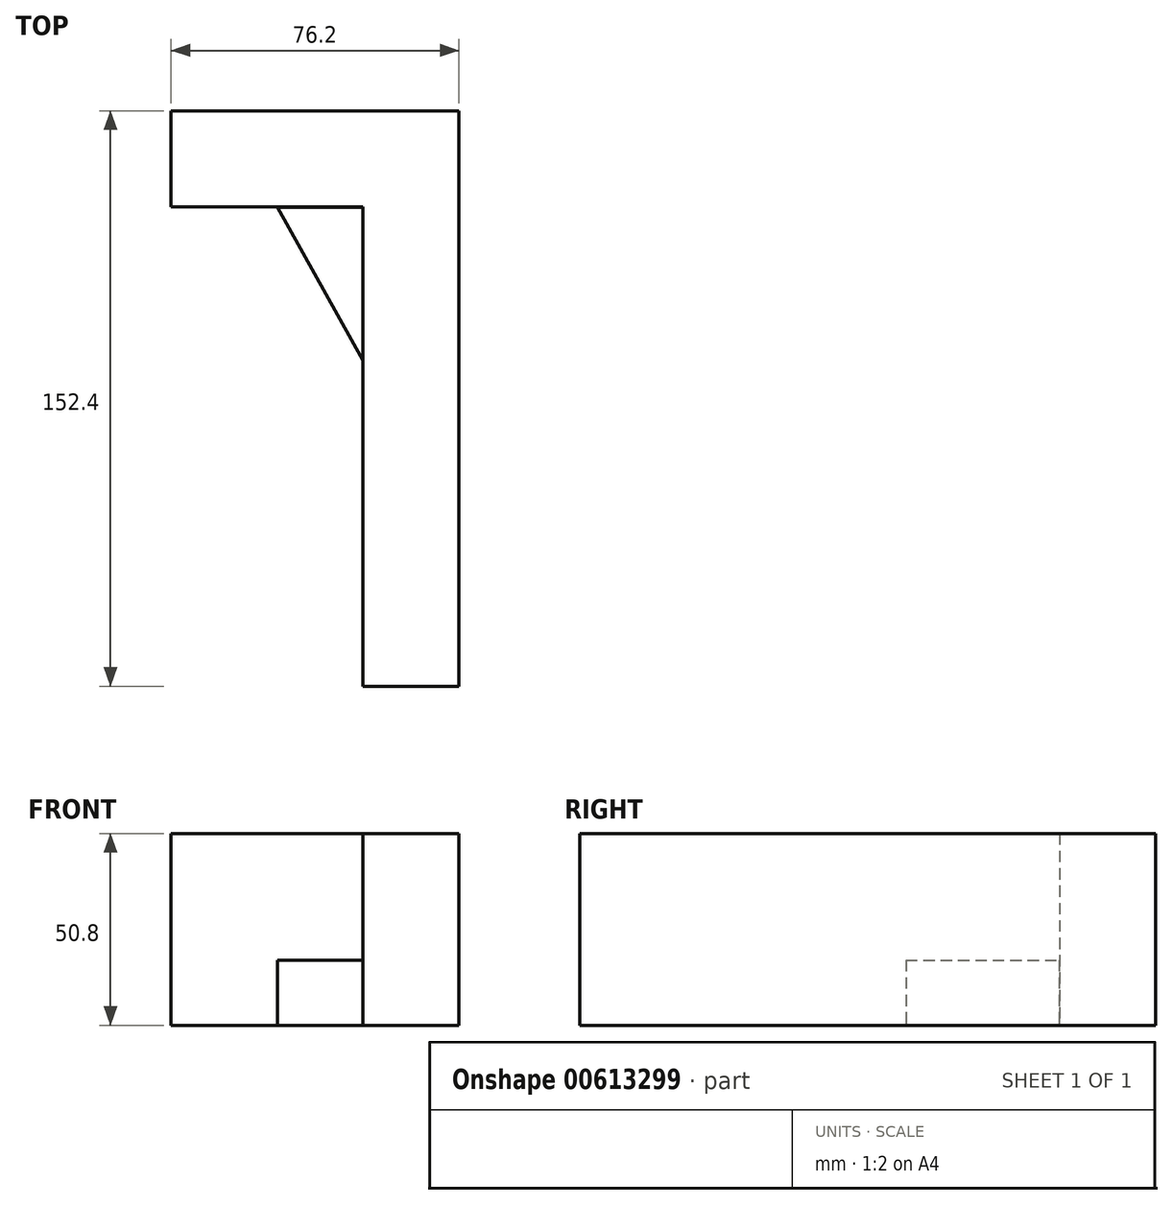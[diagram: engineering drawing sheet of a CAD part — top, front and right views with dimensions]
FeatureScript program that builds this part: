
annotation { "Feature Type Name" : "Feature", "Feature Type Description" : "" }
export const myFeature = defineFeature(function(context is Context, id is Id, definition is map)
    precondition{}
    {
        {
            var Q0;
            Q0=qCreatedBy(makeId("Top.planeOp"),FACE);
            var sketch = newSketch(context, id + "F0", { "sketchPlane" : qUnion([Q0])});
            skLineSegment(sketch, "E0", {"start": v(0, -47.08) * mm, "end": v(25.4, -47.08) * mm});
            skLineSegment(sketch, "E1", {"start": v(25.4, -47.08) * mm, "end": v(25.4, 105.32) * mm});
            skLineSegment(sketch, "E2", {"start": v(25.4, 105.32) * mm, "end": v(-50.8, 105.32) * mm});
            skLineSegment(sketch, "E3", {"start": v(-50.8, 105.32) * mm, "end": v(-50.8, 79.92) * mm});
            skLineSegment(sketch, "E4", {"start": v(-50.8, 79.92) * mm, "end": v(0, 79.92) * mm});
            skLineSegment(sketch, "E5", {"start": v(0, 79.92) * mm, "end": v(0, -47.08) * mm});
            skSolve(sketch);
        }
        {
            var Q0;
            Q0=makeQuery(id+"F0.imprint","IMPRINT",FACE,{"disambiguationData":[TD([[makeQuery(id+"F0.imprint","IMPRINT",EDGE,{"derivedFrom":sQuery(id+"F0.wireOp",EDGE,"E0")}),1.0]])]});
            extrude(context, id + "F1", {"entities" : qUnion([Q0]), "depth" : 50.8 * mm, "offsetDistance" : 25.4 * mm});
        }
        {
            var Q0;
            Q0=qCreatedBy(makeId("Top.planeOp"),FACE);
            var sketch = newSketch(context, id + "F2", { "sketchPlane" : qUnion([Q0])});
            skLineSegment(sketch, "E6", {"start": v(-22.66, 79.76) * mm, "end": v(0, 39.22) * mm});
            skLineSegment(sketch, "E7", {"start": v(-22.66, 79.76) * mm, "end": v(0, 79.76) * mm});
            skLineSegment(sketch, "E8", {"start": v(0, 39.22) * mm, "end": v(0, 79.76) * mm});
            skSolve(sketch);
        }
        {
            var Q0;
            Q0=makeQuery(id+"F2.imprint","IMPRINT",FACE,{"disambiguationData":[TD([[makeQuery(id+"F2.imprint","IMPRINT",EDGE,{"derivedFrom":sQuery(id+"F2.wireOp",EDGE,"E6")}),1.0]])]});
            extrude(context, id + "F3", {"entities" : qUnion([Q0]), "operationType" : NewBodyOperationType.ADD, "depth" : 17.27 * mm, "offsetDistance" : 25.4 * mm});
        }
    });
